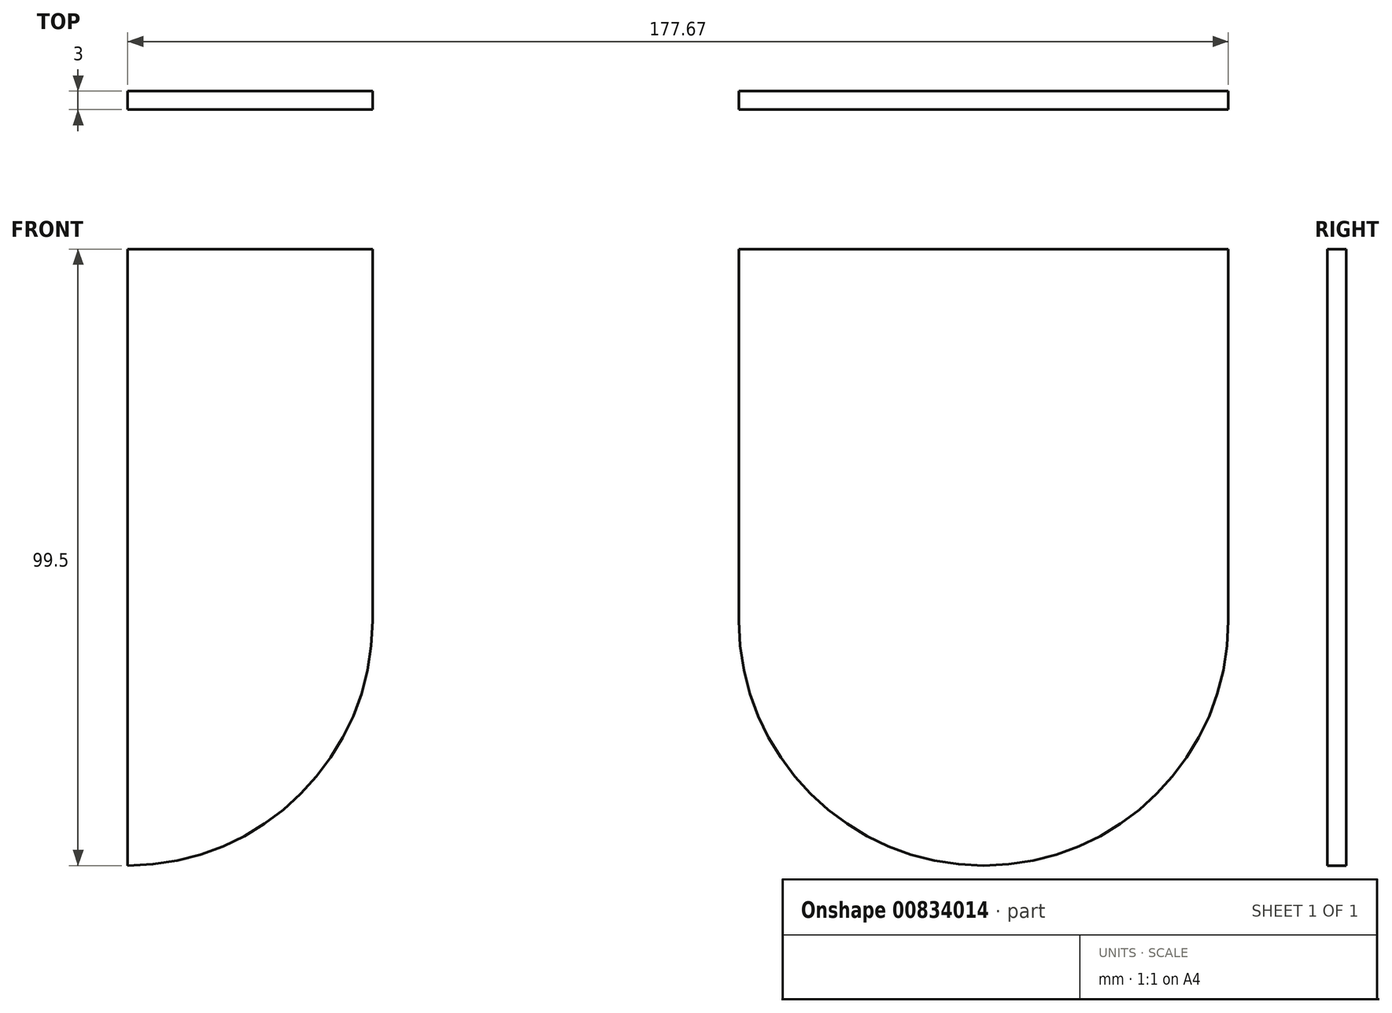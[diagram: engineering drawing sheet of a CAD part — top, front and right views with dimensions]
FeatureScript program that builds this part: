
annotation { "Feature Type Name" : "Feature", "Feature Type Description" : "" }
export const myFeature = defineFeature(function(context is Context, id is Id, definition is map)
    precondition{}
    {
        {
            var Q0;
            Q0=qCreatedBy(makeId("Front.planeOp"),FACE);
            var sketch = newSketch(context, id + "F0", { "sketchPlane" : qUnion([Q0])});
            skArc(sketch, "E0", {"start": v(-39.5, 0) * mm, "mid": v(0, -39.5) * mm, "end": v(39.5, 0) * mm});
            skLineSegment(sketch, "E1.left", {"start": v(-39.5, 60) * mm, "end": v(-39.5, 0) * mm});
            skLineSegment(sketch, "E1.right", {"start": v(39.5, 60) * mm, "end": v(39.5, 0) * mm});
            skArc(sketch, "E2", {"start": v(-138.17, -39.5) * mm, "mid": v(-110.24, -27.93) * mm, "end": v(-98.67, 0) * mm});
            skLineSegment(sketch, "E3.right", {"start": v(-98.67, 60) * mm, "end": v(-98.67, 0) * mm});
            skLineSegment(sketch, "E4", {"start": v(-138.17, 0) * mm, "end": v(-138.17, 60) * mm});
            skLineSegment(sketch, "E5", {"start": v(-138.17, 0) * mm, "end": v(-138.17, -39.5) * mm});
            skPoint(sketch, "E6.orphan", {"position": v(-177.67, 140) * mm});
            skLineSegment(sketch, "E7", {"start": v(-138.17, 60) * mm, "end": v(-98.67, 60) * mm});
            skPoint(sketch, "E3.bottom.start.orphan", {"position": v(-138.17, 140) * mm});
            skPoint(sketch, "E8.orphan", {"position": v(-98.67, 140) * mm});
            skLineSegment(sketch, "E9.trimOffspring", {"start": v(-39.5, 60) * mm, "end": v(39.5, 60) * mm});
            skSolve(sketch);
        }
        {
            var Q0;
            Q0=makeQuery(id+"F0.imprint","IMPRINT",FACE,{"disambiguationData":[TD([[makeQuery(id+"F0.imprint","IMPRINT",EDGE,{"derivedFrom":sQuery(id+"F0.wireOp",EDGE,"E0")}),1.0]])]});
            extrude(context, id + "F1", {"entities" : qUnion([Q0]), "depth" : 3 * mm, "offsetDistance" : 25 * mm});
        }
        {
            var Q0;
            Q0 = qSketchRegion(id + "F0", true);
            extrude(context, id + "F2", {"entities" : qUnion([Q0]), "operationType" : NewBodyOperationType.ADD, "depth" : 3 * mm, "offsetDistance" : 25 * mm});
        }
    });
